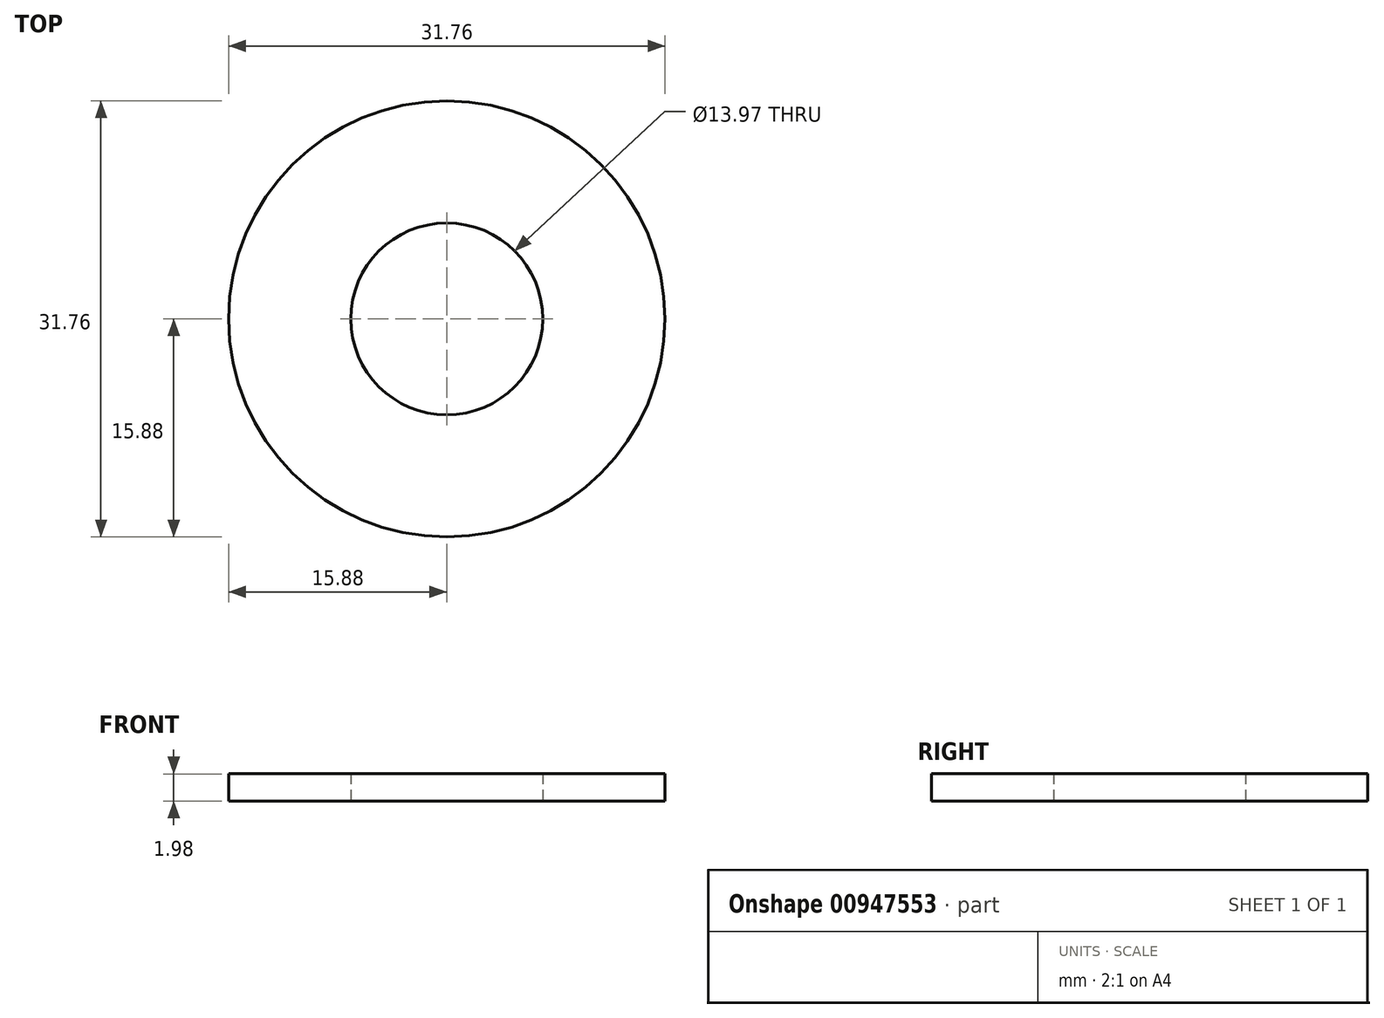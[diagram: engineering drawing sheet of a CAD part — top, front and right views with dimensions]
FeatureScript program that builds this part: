
annotation { "Feature Type Name" : "Feature", "Feature Type Description" : "" }
export const myFeature = defineFeature(function(context is Context, id is Id, definition is map)
    precondition{}
    {
        {
            var Q0;
            Q0=qCreatedBy(makeId("Top.planeOp"),FACE);
            var sketch = newSketch(context, id + "F0", { "sketchPlane" : qUnion([Q0])});
            skCircle(sketch, "E0", {"center": v(0, 0) * mm, "radius": 15.88 * mm});
            skCircle(sketch, "E1", {"center": v(0, 0) * mm, "radius": 6.99 * mm});
            skSolve(sketch);
        }
        {
            var Q0;
            Q0 = qSketchRegion(id + "F0", true);
            extrude(context, id + "F1", {"entities" : qUnion([Q0]), "depth" : 1.98 * mm, "offsetDistance" : 25.4 * mm});
        }
    });
